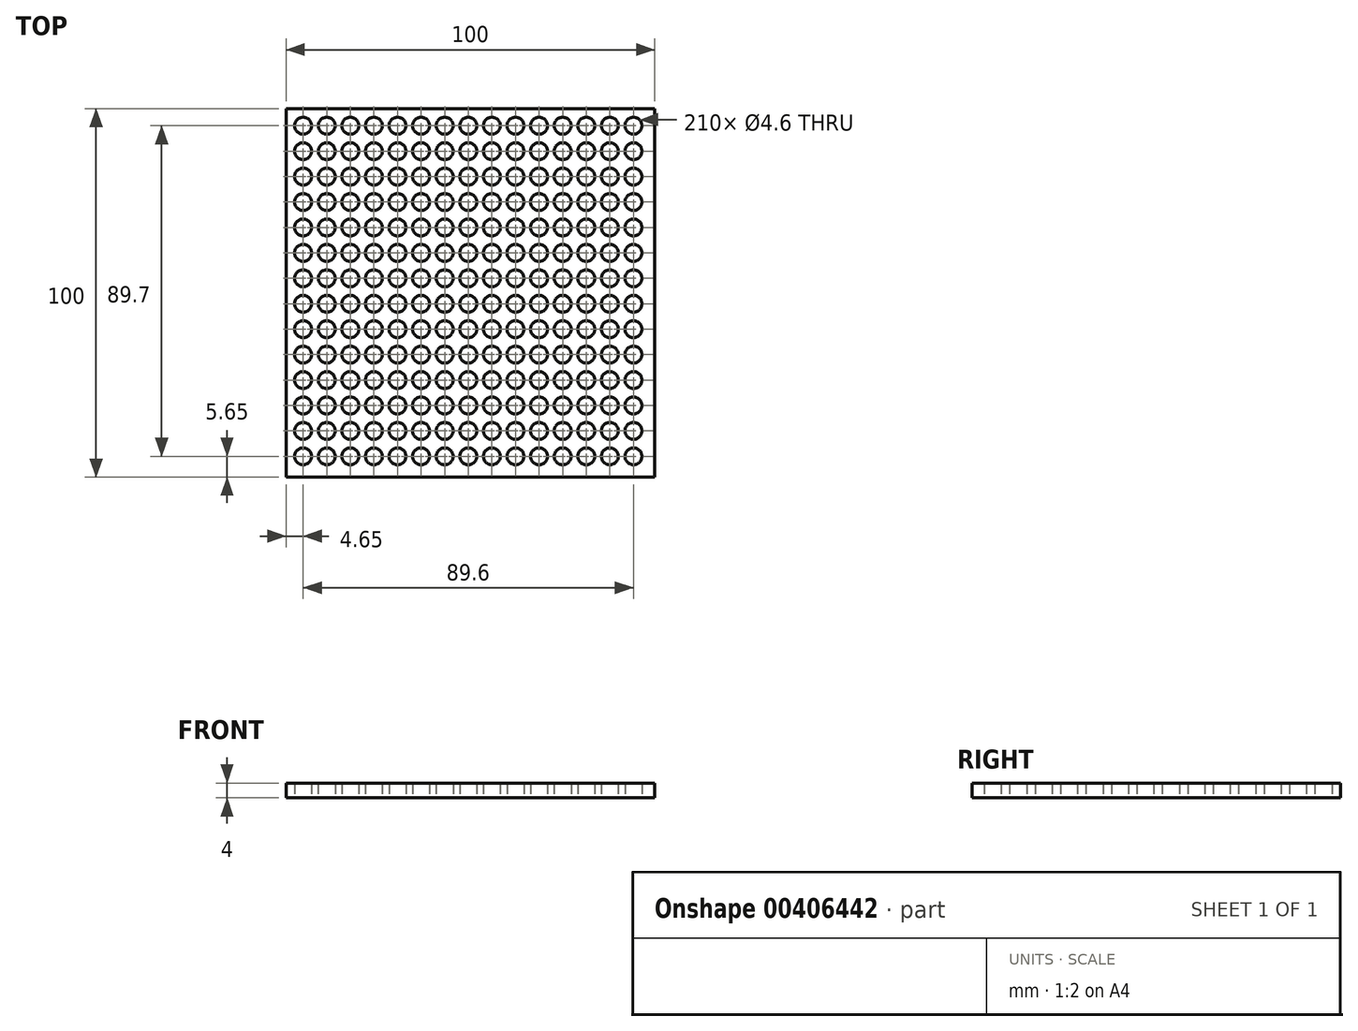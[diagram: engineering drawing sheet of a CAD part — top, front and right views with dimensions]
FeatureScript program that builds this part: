
annotation { "Feature Type Name" : "Feature", "Feature Type Description" : "" }
export const myFeature = defineFeature(function(context is Context, id is Id, definition is map)
    precondition{}
    {
        {
            var Q0;
            Q0=qCreatedBy(makeId("Top.planeOp"),FACE);
            var sketch = newSketch(context, id + "F0", { "sketchPlane" : qUnion([Q0])});
            skLineSegment(sketch, "E0.bottom", {"start": v(50, 50) * mm, "end": v(-50, 50) * mm});
            skLineSegment(sketch, "E0.top", {"start": v(50, -50) * mm, "end": v(-50, -50) * mm});
            skLineSegment(sketch, "E0.left", {"start": v(50, 50) * mm, "end": v(50, -50) * mm});
            skLineSegment(sketch, "E0.right", {"start": v(-50, 50) * mm, "end": v(-50, -50) * mm});
            skPoint(sketch, "E0.middle", {"position": v(0, 0) * mm});
            skCircle(sketch, "E1", {"center": v(-45.35, 45.35) * mm, "radius": 2.3 * mm});
            skCircle(sketch, "E2.0.1.0", {"center": v(-45.35, 38.45) * mm, "radius": 2.3 * mm});
            skCircle(sketch, "E2.0.2.0", {"center": v(-45.35, 31.55) * mm, "radius": 2.3 * mm});
            skCircle(sketch, "E2.0.3.0", {"center": v(-45.35, 24.65) * mm, "radius": 2.3 * mm});
            skCircle(sketch, "E2.0.4.0", {"center": v(-45.35, 17.75) * mm, "radius": 2.3 * mm});
            skCircle(sketch, "E2.0.5.0", {"center": v(-45.35, 10.85) * mm, "radius": 2.3 * mm});
            skCircle(sketch, "E2.0.6.0", {"center": v(-45.35, 3.95) * mm, "radius": 2.3 * mm});
            skCircle(sketch, "E2.0.7.0", {"center": v(-45.35, -2.95) * mm, "radius": 2.3 * mm});
            skCircle(sketch, "E2.0.8.0", {"center": v(-45.35, -9.85) * mm, "radius": 2.3 * mm});
            skCircle(sketch, "E2.0.9.0", {"center": v(-45.35, -16.75) * mm, "radius": 2.3 * mm});
            skCircle(sketch, "E2.0.10.0", {"center": v(-45.35, -23.65) * mm, "radius": 2.3 * mm});
            skCircle(sketch, "E2.0.11.0", {"center": v(-45.35, -30.55) * mm, "radius": 2.3 * mm});
            skCircle(sketch, "E2.0.12.0", {"center": v(-45.35, -37.45) * mm, "radius": 2.3 * mm});
            skCircle(sketch, "E2.0.13.0", {"center": v(-45.35, -44.35) * mm, "radius": 2.3 * mm});
            skCircle(sketch, "E2.1.0.0", {"center": v(-38.95, 45.35) * mm, "radius": 2.3 * mm});
            skCircle(sketch, "E2.1.1.0", {"center": v(-38.95, 38.45) * mm, "radius": 2.3 * mm});
            skCircle(sketch, "E2.1.2.0", {"center": v(-38.95, 31.55) * mm, "radius": 2.3 * mm});
            skCircle(sketch, "E2.1.3.0", {"center": v(-38.95, 24.65) * mm, "radius": 2.3 * mm});
            skCircle(sketch, "E2.1.4.0", {"center": v(-38.95, 17.75) * mm, "radius": 2.3 * mm});
            skCircle(sketch, "E2.1.5.0", {"center": v(-38.95, 10.85) * mm, "radius": 2.3 * mm});
            skCircle(sketch, "E2.1.6.0", {"center": v(-38.95, 3.95) * mm, "radius": 2.3 * mm});
            skCircle(sketch, "E2.1.7.0", {"center": v(-38.95, -2.95) * mm, "radius": 2.3 * mm});
            skCircle(sketch, "E2.1.8.0", {"center": v(-38.95, -9.85) * mm, "radius": 2.3 * mm});
            skCircle(sketch, "E2.1.9.0", {"center": v(-38.95, -16.75) * mm, "radius": 2.3 * mm});
            skCircle(sketch, "E2.1.10.0", {"center": v(-38.95, -23.65) * mm, "radius": 2.3 * mm});
            skCircle(sketch, "E2.1.11.0", {"center": v(-38.95, -30.55) * mm, "radius": 2.3 * mm});
            skCircle(sketch, "E2.1.12.0", {"center": v(-38.95, -37.45) * mm, "radius": 2.3 * mm});
            skCircle(sketch, "E2.1.13.0", {"center": v(-38.95, -44.35) * mm, "radius": 2.3 * mm});
            skCircle(sketch, "E2.2.0.0", {"center": v(-32.55, 45.35) * mm, "radius": 2.3 * mm});
            skCircle(sketch, "E2.2.1.0", {"center": v(-32.55, 38.45) * mm, "radius": 2.3 * mm});
            skCircle(sketch, "E2.2.2.0", {"center": v(-32.55, 31.55) * mm, "radius": 2.3 * mm});
            skCircle(sketch, "E2.2.3.0", {"center": v(-32.55, 24.65) * mm, "radius": 2.3 * mm});
            skCircle(sketch, "E2.2.4.0", {"center": v(-32.55, 17.75) * mm, "radius": 2.3 * mm});
            skCircle(sketch, "E2.2.5.0", {"center": v(-32.55, 10.85) * mm, "radius": 2.3 * mm});
            skCircle(sketch, "E2.2.6.0", {"center": v(-32.55, 3.95) * mm, "radius": 2.3 * mm});
            skCircle(sketch, "E2.2.7.0", {"center": v(-32.55, -2.95) * mm, "radius": 2.3 * mm});
            skCircle(sketch, "E2.2.8.0", {"center": v(-32.55, -9.85) * mm, "radius": 2.3 * mm});
            skCircle(sketch, "E2.2.9.0", {"center": v(-32.55, -16.75) * mm, "radius": 2.3 * mm});
            skCircle(sketch, "E2.2.10.0", {"center": v(-32.55, -23.65) * mm, "radius": 2.3 * mm});
            skCircle(sketch, "E2.2.11.0", {"center": v(-32.55, -30.55) * mm, "radius": 2.3 * mm});
            skCircle(sketch, "E2.2.12.0", {"center": v(-32.55, -37.45) * mm, "radius": 2.3 * mm});
            skCircle(sketch, "E2.2.13.0", {"center": v(-32.55, -44.35) * mm, "radius": 2.3 * mm});
            skCircle(sketch, "E2.3.0.0", {"center": v(-26.15, 45.35) * mm, "radius": 2.3 * mm});
            skCircle(sketch, "E2.3.1.0", {"center": v(-26.15, 38.45) * mm, "radius": 2.3 * mm});
            skCircle(sketch, "E2.3.2.0", {"center": v(-26.15, 31.55) * mm, "radius": 2.3 * mm});
            skCircle(sketch, "E2.3.3.0", {"center": v(-26.15, 24.65) * mm, "radius": 2.3 * mm});
            skCircle(sketch, "E2.3.4.0", {"center": v(-26.15, 17.75) * mm, "radius": 2.3 * mm});
            skCircle(sketch, "E2.3.5.0", {"center": v(-26.15, 10.85) * mm, "radius": 2.3 * mm});
            skCircle(sketch, "E2.3.6.0", {"center": v(-26.15, 3.95) * mm, "radius": 2.3 * mm});
            skCircle(sketch, "E2.3.7.0", {"center": v(-26.15, -2.95) * mm, "radius": 2.3 * mm});
            skCircle(sketch, "E2.3.8.0", {"center": v(-26.15, -9.85) * mm, "radius": 2.3 * mm});
            skCircle(sketch, "E2.3.9.0", {"center": v(-26.15, -16.75) * mm, "radius": 2.3 * mm});
            skCircle(sketch, "E2.3.10.0", {"center": v(-26.15, -23.65) * mm, "radius": 2.3 * mm});
            skCircle(sketch, "E2.3.11.0", {"center": v(-26.15, -30.55) * mm, "radius": 2.3 * mm});
            skCircle(sketch, "E2.3.12.0", {"center": v(-26.15, -37.45) * mm, "radius": 2.3 * mm});
            skCircle(sketch, "E2.3.13.0", {"center": v(-26.15, -44.35) * mm, "radius": 2.3 * mm});
            skCircle(sketch, "E2.4.0.0", {"center": v(-19.75, 45.35) * mm, "radius": 2.3 * mm});
            skCircle(sketch, "E2.4.1.0", {"center": v(-19.75, 38.45) * mm, "radius": 2.3 * mm});
            skCircle(sketch, "E2.4.2.0", {"center": v(-19.75, 31.55) * mm, "radius": 2.3 * mm});
            skCircle(sketch, "E2.4.3.0", {"center": v(-19.75, 24.65) * mm, "radius": 2.3 * mm});
            skCircle(sketch, "E2.4.4.0", {"center": v(-19.75, 17.75) * mm, "radius": 2.3 * mm});
            skCircle(sketch, "E2.4.5.0", {"center": v(-19.75, 10.85) * mm, "radius": 2.3 * mm});
            skCircle(sketch, "E2.4.6.0", {"center": v(-19.75, 3.95) * mm, "radius": 2.3 * mm});
            skCircle(sketch, "E2.4.7.0", {"center": v(-19.75, -2.95) * mm, "radius": 2.3 * mm});
            skCircle(sketch, "E2.4.8.0", {"center": v(-19.75, -9.85) * mm, "radius": 2.3 * mm});
            skCircle(sketch, "E2.4.9.0", {"center": v(-19.75, -16.75) * mm, "radius": 2.3 * mm});
            skCircle(sketch, "E2.4.10.0", {"center": v(-19.75, -23.65) * mm, "radius": 2.3 * mm});
            skCircle(sketch, "E2.4.11.0", {"center": v(-19.75, -30.55) * mm, "radius": 2.3 * mm});
            skCircle(sketch, "E2.4.12.0", {"center": v(-19.75, -37.45) * mm, "radius": 2.3 * mm});
            skCircle(sketch, "E2.4.13.0", {"center": v(-19.75, -44.35) * mm, "radius": 2.3 * mm});
            skCircle(sketch, "E2.5.0.0", {"center": v(-13.35, 45.35) * mm, "radius": 2.3 * mm});
            skCircle(sketch, "E2.5.1.0", {"center": v(-13.35, 38.45) * mm, "radius": 2.3 * mm});
            skCircle(sketch, "E2.5.2.0", {"center": v(-13.35, 31.55) * mm, "radius": 2.3 * mm});
            skCircle(sketch, "E2.5.3.0", {"center": v(-13.35, 24.65) * mm, "radius": 2.3 * mm});
            skCircle(sketch, "E2.5.4.0", {"center": v(-13.35, 17.75) * mm, "radius": 2.3 * mm});
            skCircle(sketch, "E2.5.5.0", {"center": v(-13.35, 10.85) * mm, "radius": 2.3 * mm});
            skCircle(sketch, "E2.5.6.0", {"center": v(-13.35, 3.95) * mm, "radius": 2.3 * mm});
            skCircle(sketch, "E2.5.7.0", {"center": v(-13.35, -2.95) * mm, "radius": 2.3 * mm});
            skCircle(sketch, "E2.5.8.0", {"center": v(-13.35, -9.85) * mm, "radius": 2.3 * mm});
            skCircle(sketch, "E2.5.9.0", {"center": v(-13.35, -16.75) * mm, "radius": 2.3 * mm});
            skCircle(sketch, "E2.5.10.0", {"center": v(-13.35, -23.65) * mm, "radius": 2.3 * mm});
            skCircle(sketch, "E2.5.11.0", {"center": v(-13.35, -30.55) * mm, "radius": 2.3 * mm});
            skCircle(sketch, "E2.5.12.0", {"center": v(-13.35, -37.45) * mm, "radius": 2.3 * mm});
            skCircle(sketch, "E2.5.13.0", {"center": v(-13.35, -44.35) * mm, "radius": 2.3 * mm});
            skCircle(sketch, "E2.6.0.0", {"center": v(-6.95, 45.35) * mm, "radius": 2.3 * mm});
            skCircle(sketch, "E2.6.1.0", {"center": v(-6.95, 38.45) * mm, "radius": 2.3 * mm});
            skCircle(sketch, "E2.6.2.0", {"center": v(-6.95, 31.55) * mm, "radius": 2.3 * mm});
            skCircle(sketch, "E2.6.3.0", {"center": v(-6.95, 24.65) * mm, "radius": 2.3 * mm});
            skCircle(sketch, "E2.6.4.0", {"center": v(-6.95, 17.75) * mm, "radius": 2.3 * mm});
            skCircle(sketch, "E2.6.5.0", {"center": v(-6.95, 10.85) * mm, "radius": 2.3 * mm});
            skCircle(sketch, "E2.6.6.0", {"center": v(-6.95, 3.95) * mm, "radius": 2.3 * mm});
            skCircle(sketch, "E2.6.7.0", {"center": v(-6.95, -2.95) * mm, "radius": 2.3 * mm});
            skCircle(sketch, "E2.6.8.0", {"center": v(-6.95, -9.85) * mm, "radius": 2.3 * mm});
            skCircle(sketch, "E2.6.9.0", {"center": v(-6.95, -16.75) * mm, "radius": 2.3 * mm});
            skCircle(sketch, "E2.6.10.0", {"center": v(-6.95, -23.65) * mm, "radius": 2.3 * mm});
            skCircle(sketch, "E2.6.11.0", {"center": v(-6.95, -30.55) * mm, "radius": 2.3 * mm});
            skCircle(sketch, "E2.6.12.0", {"center": v(-6.95, -37.45) * mm, "radius": 2.3 * mm});
            skCircle(sketch, "E2.6.13.0", {"center": v(-6.95, -44.35) * mm, "radius": 2.3 * mm});
            skCircle(sketch, "E2.7.0.0", {"center": v(-0.55, 45.35) * mm, "radius": 2.3 * mm});
            skCircle(sketch, "E2.7.1.0", {"center": v(-0.55, 38.45) * mm, "radius": 2.3 * mm});
            skCircle(sketch, "E2.7.2.0", {"center": v(-0.55, 31.55) * mm, "radius": 2.3 * mm});
            skCircle(sketch, "E2.7.3.0", {"center": v(-0.55, 24.65) * mm, "radius": 2.3 * mm});
            skCircle(sketch, "E2.7.4.0", {"center": v(-0.55, 17.75) * mm, "radius": 2.3 * mm});
            skCircle(sketch, "E2.7.5.0", {"center": v(-0.55, 10.85) * mm, "radius": 2.3 * mm});
            skCircle(sketch, "E2.7.6.0", {"center": v(-0.55, 3.95) * mm, "radius": 2.3 * mm});
            skCircle(sketch, "E2.7.7.0", {"center": v(-0.55, -2.95) * mm, "radius": 2.3 * mm});
            skCircle(sketch, "E2.7.8.0", {"center": v(-0.55, -9.85) * mm, "radius": 2.3 * mm});
            skCircle(sketch, "E2.7.9.0", {"center": v(-0.55, -16.75) * mm, "radius": 2.3 * mm});
            skCircle(sketch, "E2.7.10.0", {"center": v(-0.55, -23.65) * mm, "radius": 2.3 * mm});
            skCircle(sketch, "E2.7.11.0", {"center": v(-0.55, -30.55) * mm, "radius": 2.3 * mm});
            skCircle(sketch, "E2.7.12.0", {"center": v(-0.55, -37.45) * mm, "radius": 2.3 * mm});
            skCircle(sketch, "E2.7.13.0", {"center": v(-0.55, -44.35) * mm, "radius": 2.3 * mm});
            skCircle(sketch, "E2.8.0.0", {"center": v(5.85, 45.35) * mm, "radius": 2.3 * mm});
            skCircle(sketch, "E2.8.1.0", {"center": v(5.85, 38.45) * mm, "radius": 2.3 * mm});
            skCircle(sketch, "E2.8.2.0", {"center": v(5.85, 31.55) * mm, "radius": 2.3 * mm});
            skCircle(sketch, "E2.8.3.0", {"center": v(5.85, 24.65) * mm, "radius": 2.3 * mm});
            skCircle(sketch, "E2.8.4.0", {"center": v(5.85, 17.75) * mm, "radius": 2.3 * mm});
            skCircle(sketch, "E2.8.5.0", {"center": v(5.85, 10.85) * mm, "radius": 2.3 * mm});
            skCircle(sketch, "E2.8.6.0", {"center": v(5.85, 3.95) * mm, "radius": 2.3 * mm});
            skCircle(sketch, "E2.8.7.0", {"center": v(5.85, -2.95) * mm, "radius": 2.3 * mm});
            skCircle(sketch, "E2.8.8.0", {"center": v(5.85, -9.85) * mm, "radius": 2.3 * mm});
            skCircle(sketch, "E2.8.9.0", {"center": v(5.85, -16.75) * mm, "radius": 2.3 * mm});
            skCircle(sketch, "E2.8.10.0", {"center": v(5.85, -23.65) * mm, "radius": 2.3 * mm});
            skCircle(sketch, "E2.8.11.0", {"center": v(5.85, -30.55) * mm, "radius": 2.3 * mm});
            skCircle(sketch, "E2.8.12.0", {"center": v(5.85, -37.45) * mm, "radius": 2.3 * mm});
            skCircle(sketch, "E2.8.13.0", {"center": v(5.85, -44.35) * mm, "radius": 2.3 * mm});
            skCircle(sketch, "E2.9.0.0", {"center": v(12.25, 45.35) * mm, "radius": 2.3 * mm});
            skCircle(sketch, "E2.9.1.0", {"center": v(12.25, 38.45) * mm, "radius": 2.3 * mm});
            skCircle(sketch, "E2.9.2.0", {"center": v(12.25, 31.55) * mm, "radius": 2.3 * mm});
            skCircle(sketch, "E2.9.3.0", {"center": v(12.25, 24.65) * mm, "radius": 2.3 * mm});
            skCircle(sketch, "E2.9.4.0", {"center": v(12.25, 17.75) * mm, "radius": 2.3 * mm});
            skCircle(sketch, "E2.9.5.0", {"center": v(12.25, 10.85) * mm, "radius": 2.3 * mm});
            skCircle(sketch, "E2.9.6.0", {"center": v(12.25, 3.95) * mm, "radius": 2.3 * mm});
            skCircle(sketch, "E2.9.7.0", {"center": v(12.25, -2.95) * mm, "radius": 2.3 * mm});
            skCircle(sketch, "E2.9.8.0", {"center": v(12.25, -9.85) * mm, "radius": 2.3 * mm});
            skCircle(sketch, "E2.9.9.0", {"center": v(12.25, -16.75) * mm, "radius": 2.3 * mm});
            skCircle(sketch, "E2.9.10.0", {"center": v(12.25, -23.65) * mm, "radius": 2.3 * mm});
            skCircle(sketch, "E2.9.11.0", {"center": v(12.25, -30.55) * mm, "radius": 2.3 * mm});
            skCircle(sketch, "E2.9.12.0", {"center": v(12.25, -37.45) * mm, "radius": 2.3 * mm});
            skCircle(sketch, "E2.9.13.0", {"center": v(12.25, -44.35) * mm, "radius": 2.3 * mm});
            skCircle(sketch, "E2.10.0.0", {"center": v(18.65, 45.35) * mm, "radius": 2.3 * mm});
            skCircle(sketch, "E2.10.1.0", {"center": v(18.65, 38.45) * mm, "radius": 2.3 * mm});
            skCircle(sketch, "E2.10.2.0", {"center": v(18.65, 31.55) * mm, "radius": 2.3 * mm});
            skCircle(sketch, "E2.10.3.0", {"center": v(18.65, 24.65) * mm, "radius": 2.3 * mm});
            skCircle(sketch, "E2.10.4.0", {"center": v(18.65, 17.75) * mm, "radius": 2.3 * mm});
            skCircle(sketch, "E2.10.5.0", {"center": v(18.65, 10.85) * mm, "radius": 2.3 * mm});
            skCircle(sketch, "E2.10.6.0", {"center": v(18.65, 3.95) * mm, "radius": 2.3 * mm});
            skCircle(sketch, "E2.10.7.0", {"center": v(18.65, -2.95) * mm, "radius": 2.3 * mm});
            skCircle(sketch, "E2.10.8.0", {"center": v(18.65, -9.85) * mm, "radius": 2.3 * mm});
            skCircle(sketch, "E2.10.9.0", {"center": v(18.65, -16.75) * mm, "radius": 2.3 * mm});
            skCircle(sketch, "E2.10.10.0", {"center": v(18.65, -23.65) * mm, "radius": 2.3 * mm});
            skCircle(sketch, "E2.10.11.0", {"center": v(18.65, -30.55) * mm, "radius": 2.3 * mm});
            skCircle(sketch, "E2.10.12.0", {"center": v(18.65, -37.45) * mm, "radius": 2.3 * mm});
            skCircle(sketch, "E2.10.13.0", {"center": v(18.65, -44.35) * mm, "radius": 2.3 * mm});
            skCircle(sketch, "E2.11.0.0", {"center": v(25.05, 45.35) * mm, "radius": 2.3 * mm});
            skCircle(sketch, "E2.11.1.0", {"center": v(25.05, 38.45) * mm, "radius": 2.3 * mm});
            skCircle(sketch, "E2.11.2.0", {"center": v(25.05, 31.55) * mm, "radius": 2.3 * mm});
            skCircle(sketch, "E2.11.3.0", {"center": v(25.05, 24.65) * mm, "radius": 2.3 * mm});
            skCircle(sketch, "E2.11.4.0", {"center": v(25.05, 17.75) * mm, "radius": 2.3 * mm});
            skCircle(sketch, "E2.11.5.0", {"center": v(25.05, 10.85) * mm, "radius": 2.3 * mm});
            skCircle(sketch, "E2.11.6.0", {"center": v(25.05, 3.95) * mm, "radius": 2.3 * mm});
            skCircle(sketch, "E2.11.7.0", {"center": v(25.05, -2.95) * mm, "radius": 2.3 * mm});
            skCircle(sketch, "E2.11.8.0", {"center": v(25.05, -9.85) * mm, "radius": 2.3 * mm});
            skCircle(sketch, "E2.11.9.0", {"center": v(25.05, -16.75) * mm, "radius": 2.3 * mm});
            skCircle(sketch, "E2.11.10.0", {"center": v(25.05, -23.65) * mm, "radius": 2.3 * mm});
            skCircle(sketch, "E2.11.11.0", {"center": v(25.05, -30.55) * mm, "radius": 2.3 * mm});
            skCircle(sketch, "E2.11.12.0", {"center": v(25.05, -37.45) * mm, "radius": 2.3 * mm});
            skCircle(sketch, "E2.11.13.0", {"center": v(25.05, -44.35) * mm, "radius": 2.3 * mm});
            skCircle(sketch, "E2.12.0.0", {"center": v(31.45, 45.35) * mm, "radius": 2.3 * mm});
            skCircle(sketch, "E2.12.1.0", {"center": v(31.45, 38.45) * mm, "radius": 2.3 * mm});
            skCircle(sketch, "E2.12.2.0", {"center": v(31.45, 31.55) * mm, "radius": 2.3 * mm});
            skCircle(sketch, "E2.12.3.0", {"center": v(31.45, 24.65) * mm, "radius": 2.3 * mm});
            skCircle(sketch, "E2.12.4.0", {"center": v(31.45, 17.75) * mm, "radius": 2.3 * mm});
            skCircle(sketch, "E2.12.5.0", {"center": v(31.45, 10.85) * mm, "radius": 2.3 * mm});
            skCircle(sketch, "E2.12.6.0", {"center": v(31.45, 3.95) * mm, "radius": 2.3 * mm});
            skCircle(sketch, "E2.12.7.0", {"center": v(31.45, -2.95) * mm, "radius": 2.3 * mm});
            skCircle(sketch, "E2.12.8.0", {"center": v(31.45, -9.85) * mm, "radius": 2.3 * mm});
            skCircle(sketch, "E2.12.9.0", {"center": v(31.45, -16.75) * mm, "radius": 2.3 * mm});
            skCircle(sketch, "E2.12.10.0", {"center": v(31.45, -23.65) * mm, "radius": 2.3 * mm});
            skCircle(sketch, "E2.12.11.0", {"center": v(31.45, -30.55) * mm, "radius": 2.3 * mm});
            skCircle(sketch, "E2.12.12.0", {"center": v(31.45, -37.45) * mm, "radius": 2.3 * mm});
            skCircle(sketch, "E2.12.13.0", {"center": v(31.45, -44.35) * mm, "radius": 2.3 * mm});
            skCircle(sketch, "E2.13.0.0", {"center": v(37.85, 45.35) * mm, "radius": 2.3 * mm});
            skCircle(sketch, "E2.13.1.0", {"center": v(37.85, 38.45) * mm, "radius": 2.3 * mm});
            skCircle(sketch, "E2.13.2.0", {"center": v(37.85, 31.55) * mm, "radius": 2.3 * mm});
            skCircle(sketch, "E2.13.3.0", {"center": v(37.85, 24.65) * mm, "radius": 2.3 * mm});
            skCircle(sketch, "E2.13.4.0", {"center": v(37.85, 17.75) * mm, "radius": 2.3 * mm});
            skCircle(sketch, "E2.13.5.0", {"center": v(37.85, 10.85) * mm, "radius": 2.3 * mm});
            skCircle(sketch, "E2.13.6.0", {"center": v(37.85, 3.95) * mm, "radius": 2.3 * mm});
            skCircle(sketch, "E2.13.7.0", {"center": v(37.85, -2.95) * mm, "radius": 2.3 * mm});
            skCircle(sketch, "E2.13.8.0", {"center": v(37.85, -9.85) * mm, "radius": 2.3 * mm});
            skCircle(sketch, "E2.13.9.0", {"center": v(37.85, -16.75) * mm, "radius": 2.3 * mm});
            skCircle(sketch, "E2.13.10.0", {"center": v(37.85, -23.65) * mm, "radius": 2.3 * mm});
            skCircle(sketch, "E2.13.11.0", {"center": v(37.85, -30.55) * mm, "radius": 2.3 * mm});
            skCircle(sketch, "E2.13.12.0", {"center": v(37.85, -37.45) * mm, "radius": 2.3 * mm});
            skCircle(sketch, "E2.13.13.0", {"center": v(37.85, -44.35) * mm, "radius": 2.3 * mm});
            skCircle(sketch, "E2.14.0.0", {"center": v(44.25, 45.35) * mm, "radius": 2.3 * mm});
            skCircle(sketch, "E2.14.1.0", {"center": v(44.25, 38.45) * mm, "radius": 2.3 * mm});
            skCircle(sketch, "E2.14.2.0", {"center": v(44.25, 31.55) * mm, "radius": 2.3 * mm});
            skCircle(sketch, "E2.14.3.0", {"center": v(44.25, 24.65) * mm, "radius": 2.3 * mm});
            skCircle(sketch, "E2.14.4.0", {"center": v(44.25, 17.75) * mm, "radius": 2.3 * mm});
            skCircle(sketch, "E2.14.5.0", {"center": v(44.25, 10.85) * mm, "radius": 2.3 * mm});
            skCircle(sketch, "E2.14.6.0", {"center": v(44.25, 3.95) * mm, "radius": 2.3 * mm});
            skCircle(sketch, "E2.14.7.0", {"center": v(44.25, -2.95) * mm, "radius": 2.3 * mm});
            skCircle(sketch, "E2.14.8.0", {"center": v(44.25, -9.85) * mm, "radius": 2.3 * mm});
            skCircle(sketch, "E2.14.9.0", {"center": v(44.25, -16.75) * mm, "radius": 2.3 * mm});
            skCircle(sketch, "E2.14.10.0", {"center": v(44.25, -23.65) * mm, "radius": 2.3 * mm});
            skCircle(sketch, "E2.14.11.0", {"center": v(44.25, -30.55) * mm, "radius": 2.3 * mm});
            skCircle(sketch, "E2.14.12.0", {"center": v(44.25, -37.45) * mm, "radius": 2.3 * mm});
            skCircle(sketch, "E2.14.13.0", {"center": v(44.25, -44.35) * mm, "radius": 2.3 * mm});
            skLineSegment(sketch, "E2.direction1", {"start": v(-45.35, 45.35) * mm, "end": v(-38.95, 45.35) * mm, "construction": true});
            skLineSegment(sketch, "E2.direction2", {"start": v(-45.35, 45.35) * mm, "end": v(-45.35, 38.45) * mm, "construction": true});
            skSolve(sketch);
        }
        {
            var Q0;
            Q0=makeQuery(id+"F0.imprint","IMPRINT",FACE,{"disambiguationData":[TD([[makeQuery(id+"F0.imprint","IMPRINT",EDGE,{"derivedFrom":sQuery(id+"F0.wireOp",EDGE,"E0.bottom")}),1.0]])]});
            extrude(context, id + "F1", {"entities" : qUnion([Q0]), "depth" : 4 * mm});
        }
    });
